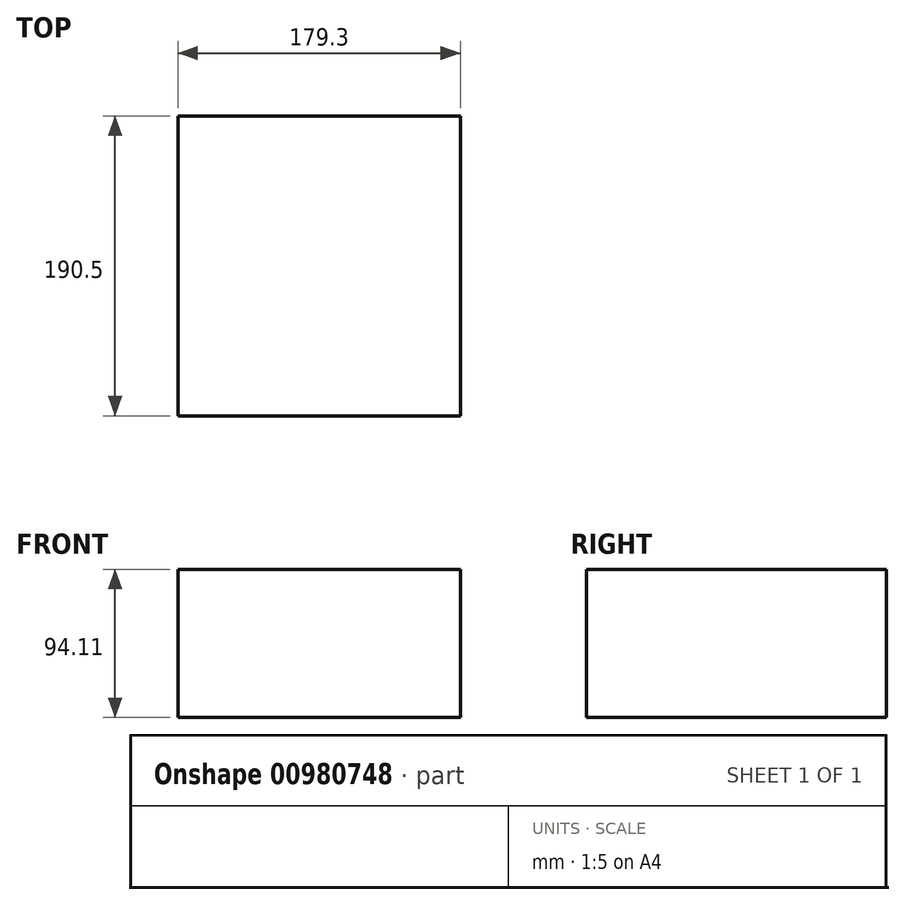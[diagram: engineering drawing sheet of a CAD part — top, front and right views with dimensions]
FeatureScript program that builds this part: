
annotation { "Feature Type Name" : "Feature", "Feature Type Description" : "" }
export const myFeature = defineFeature(function(context is Context, id is Id, definition is map)
    precondition{}
    {
        {
            var Q0;
            Q0=qCreatedBy(makeId("Front.planeOp"),FACE);
            var sketch = newSketch(context, id + "F0", { "sketchPlane" : qUnion([Q0])});
            skLineSegment(sketch, "E0.top", {"start": v(-99.72, -42.45) * mm, "end": v(79.58, -42.45) * mm});
            skLineSegment(sketch, "E0.left", {"start": v(-99.72, 56.27) * mm, "end": v(-99.72, -42.45) * mm});
            skLineSegment(sketch, "E0.right", {"start": v(79.58, 56.27) * mm, "end": v(79.58, -42.45) * mm});
            skLineSegment(sketch, "E1", {"start": v(-99.72, 51.66) * mm, "end": v(79.58, 51.66) * mm});
            skSolve(sketch);
        }
        {
            var Q0;
            Q0 = qSketchRegion(id + "F0", true);
            extrude(context, id + "F1", {"entities" : qUnion([Q0]), "depth" : 190.5 * mm, "offsetDistance" : 25.4 * mm});
        }
    });
